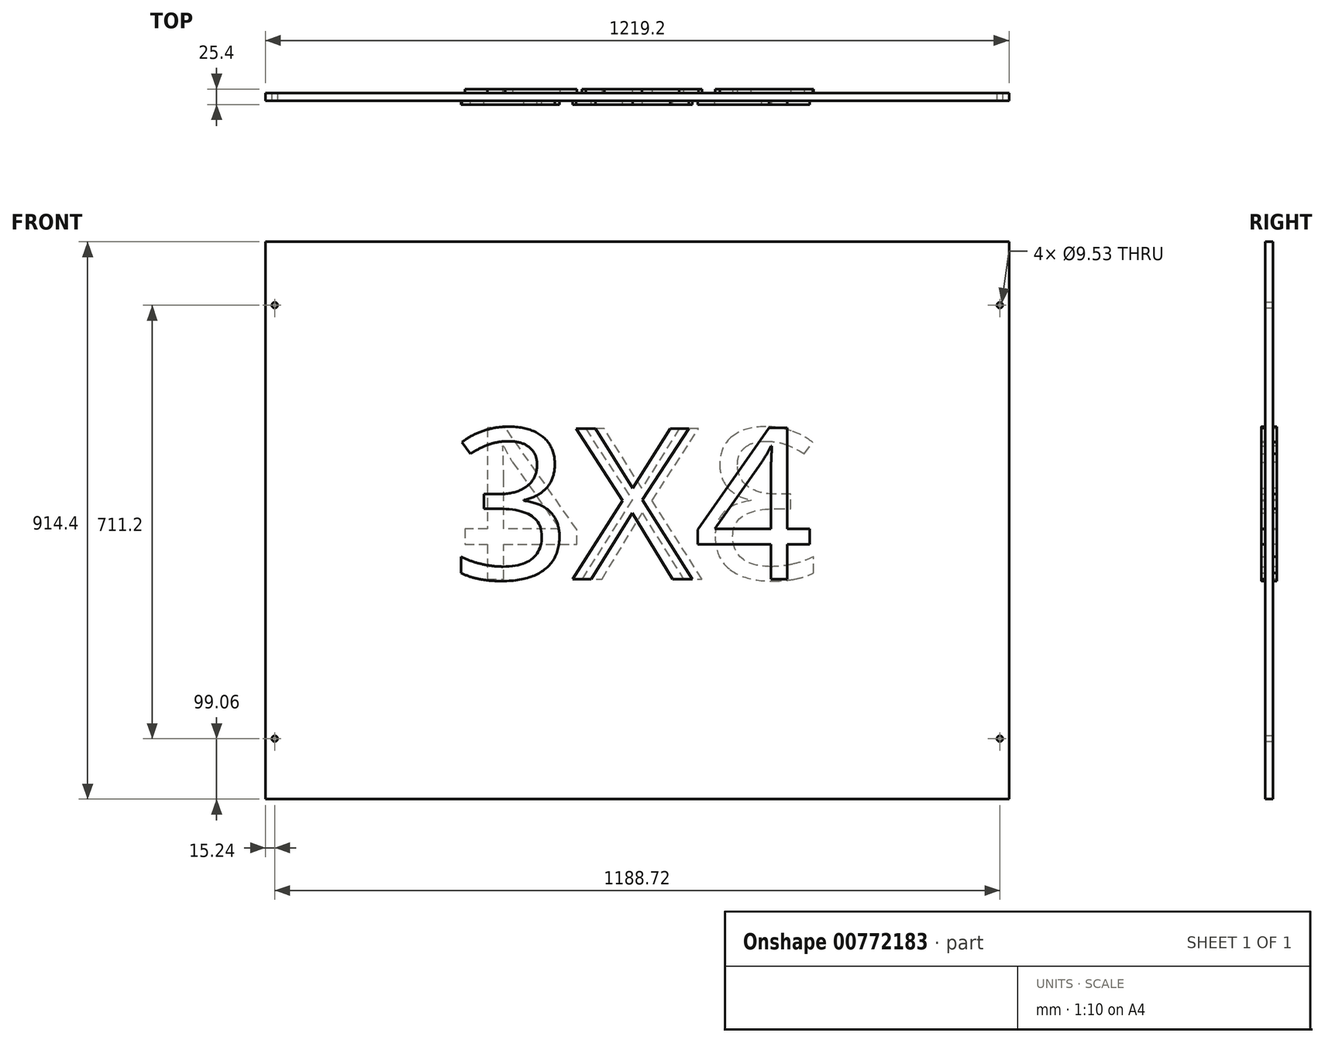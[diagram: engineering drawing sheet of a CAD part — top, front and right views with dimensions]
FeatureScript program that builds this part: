
annotation { "Feature Type Name" : "Feature", "Feature Type Description" : "" }
export const myFeature = defineFeature(function(context is Context, id is Id, definition is map)
    precondition{}
    {
        {
            var Q0;
            Q0=qCreatedBy(makeId("Front.planeOp"),FACE);
            var sketch = newSketch(context, id + "F0", { "sketchPlane" : qUnion([Q0])});
            skLineSegment(sketch, "E0.bottom", {"start": v(0, 0) * mm, "end": v(1219.2, 0) * mm});
            skLineSegment(sketch, "E0.top", {"start": v(0, 914.4) * mm, "end": v(1219.2, 914.4) * mm});
            skLineSegment(sketch, "E0.left", {"start": v(0, 0) * mm, "end": v(0, 914.4) * mm});
            skLineSegment(sketch, "E0.right", {"start": v(1219.2, 0) * mm, "end": v(1219.2, 914.4) * mm});
            skSolve(sketch);
        }
        {
            var Q0;
            Q0=makeQuery(id+"F0.imprint","IMPRINT",FACE,{"disambiguationData":[TD([[makeQuery(id+"F0.imprint","IMPRINT",EDGE,{"derivedFrom":sQuery(id+"F0.wireOp",EDGE,"E0.bottom")}),1.0]])]});
            extrude(context, id + "F1", {"entities" : qUnion([Q0]), "depth" : 12.7 * mm, "offsetDistance" : 25.4 * mm});
        }
        {
            var Q0;
            Q0=makeQuery(id+"F1.opExtrude","CAP_FACE",FACE,{"disambiguationData":[OSD([sQuery(id+"F0.wireOp",EDGE,"E0.bottom"),sQuery(id+"F0.wireOp",EDGE,"E0.top"),sQuery(id+"F0.wireOp",EDGE,"E0.left"),sQuery(id+"F0.wireOp",EDGE,"E0.right")])],"isStart":false});
            var sketch = newSketch(context, id + "F2", { "sketchPlane" : qUnion([Q0])});
            skCircle(sketch, "E1", {"center": v(15.24, 810.26) * mm, "radius": 4.76 * mm});
            skCircle(sketch, "E2", {"center": v(15.24, 99.06) * mm, "radius": 4.76 * mm});
            skCircle(sketch, "E3", {"center": v(1203.96, 810.26) * mm, "radius": 4.76 * mm});
            skCircle(sketch, "E4", {"center": v(1203.96, 99.06) * mm, "radius": 4.76 * mm});
            skSolve(sketch);
        }
        {
            var Q0;
            Q0=makeQuery(id+"F2.imprint","IMPRINT",FACE,{"disambiguationData":[TD([[makeQuery(id+"F2.imprint","IMPRINT",EDGE,{"derivedFrom":sQuery(id+"F2.wireOp",EDGE,"E3")}),1.0]])]});
            var Q1;
            Q1=makeQuery(id+"F2.imprint","IMPRINT",FACE,{"disambiguationData":[TD([[makeQuery(id+"F2.imprint","IMPRINT",EDGE,{"derivedFrom":sQuery(id+"F2.wireOp",EDGE,"E4")}),1.0]])]});
            var Q2;
            Q2=makeQuery(id+"F2.imprint","IMPRINT",FACE,{"disambiguationData":[TD([[makeQuery(id+"F2.imprint","IMPRINT",EDGE,{"derivedFrom":sQuery(id+"F2.wireOp",EDGE,"E2")}),1.0]])]});
            var Q3;
            Q3=makeQuery(id+"F2.imprint","IMPRINT",FACE,{"disambiguationData":[TD([[makeQuery(id+"F2.imprint","IMPRINT",EDGE,{"derivedFrom":sQuery(id+"F2.wireOp",EDGE,"E1")}),1.0]])]});
            extrude(context, id + "F3", {"entities" : qUnion([Q0, Q1, Q2, Q3]), "operationType" : NewBodyOperationType.REMOVE, "endBound" : BoundingType.THROUGH_ALL, "oppositeDirection" : true, "depth" : 25.4 * mm, "offsetDistance" : 25.4 * mm});
        }
        {
            var Q0;
            Q0=makeQuery(id+"F1.opExtrude","CAP_FACE",FACE,{"disambiguationData":[OSD([sQuery(id+"F0.wireOp",EDGE,"E0.bottom"),sQuery(id+"F0.wireOp",EDGE,"E0.top"),sQuery(id+"F0.wireOp",EDGE,"E0.left"),sQuery(id+"F0.wireOp",EDGE,"E0.right")])],"isStart":false});
            var sketch = newSketch(context, id + "F4", { "sketchPlane" : qUnion([Q0])});
            skText(sketch, "E5", { "text": "3X4", "fontName": "OpenSans-Regular.ttf"});
            const initialGuessF4  = {"E5": [0.3048, 0.361, 1, 0, 0.2486]};
            skSetInitialGuess(sketch, initialGuessF4);
            skSolve(sketch);
        }
        {
            var Q0;
            Q0 = qSketchRegion(id + "F4", true);
            extrude(context, id + "F5", {"entities" : qUnion([Q0]), "operationType" : NewBodyOperationType.ADD, "depth" : 6.35 * mm, "offsetDistance" : 25.4 * mm});
        }
        {
            var Q0;
            Q0=makeQuery(id+"F1.opExtrude","CAP_FACE",FACE,{"disambiguationData":[OSD([sQuery(id+"F0.wireOp",EDGE,"E0.bottom"),sQuery(id+"F0.wireOp",EDGE,"E0.top"),sQuery(id+"F0.wireOp",EDGE,"E0.left"),sQuery(id+"F0.wireOp",EDGE,"E0.right")])],"isStart":true});
            var sketch = newSketch(context, id + "F6", { "sketchPlane" : qUnion([Q0])});
            skText(sketch, "E6", { "text": "3X4", "fontName": "OpenSans-Regular.ttf"});
            const initialGuessF6  = {"E6": [-0.9144, 0.361, 1, 0, 0.2486]};
            skSetInitialGuess(sketch, initialGuessF6);
            skSolve(sketch);
        }
        {
            var Q0;
            Q0=qSketchRegion(id+"F6",true);
            extrude(context, id + "F7", {"entities" : qUnion([Q0]), "operationType" : NewBodyOperationType.ADD, "depth" : 6.35 * mm, "offsetDistance" : 25.4 * mm});
        }
    });
